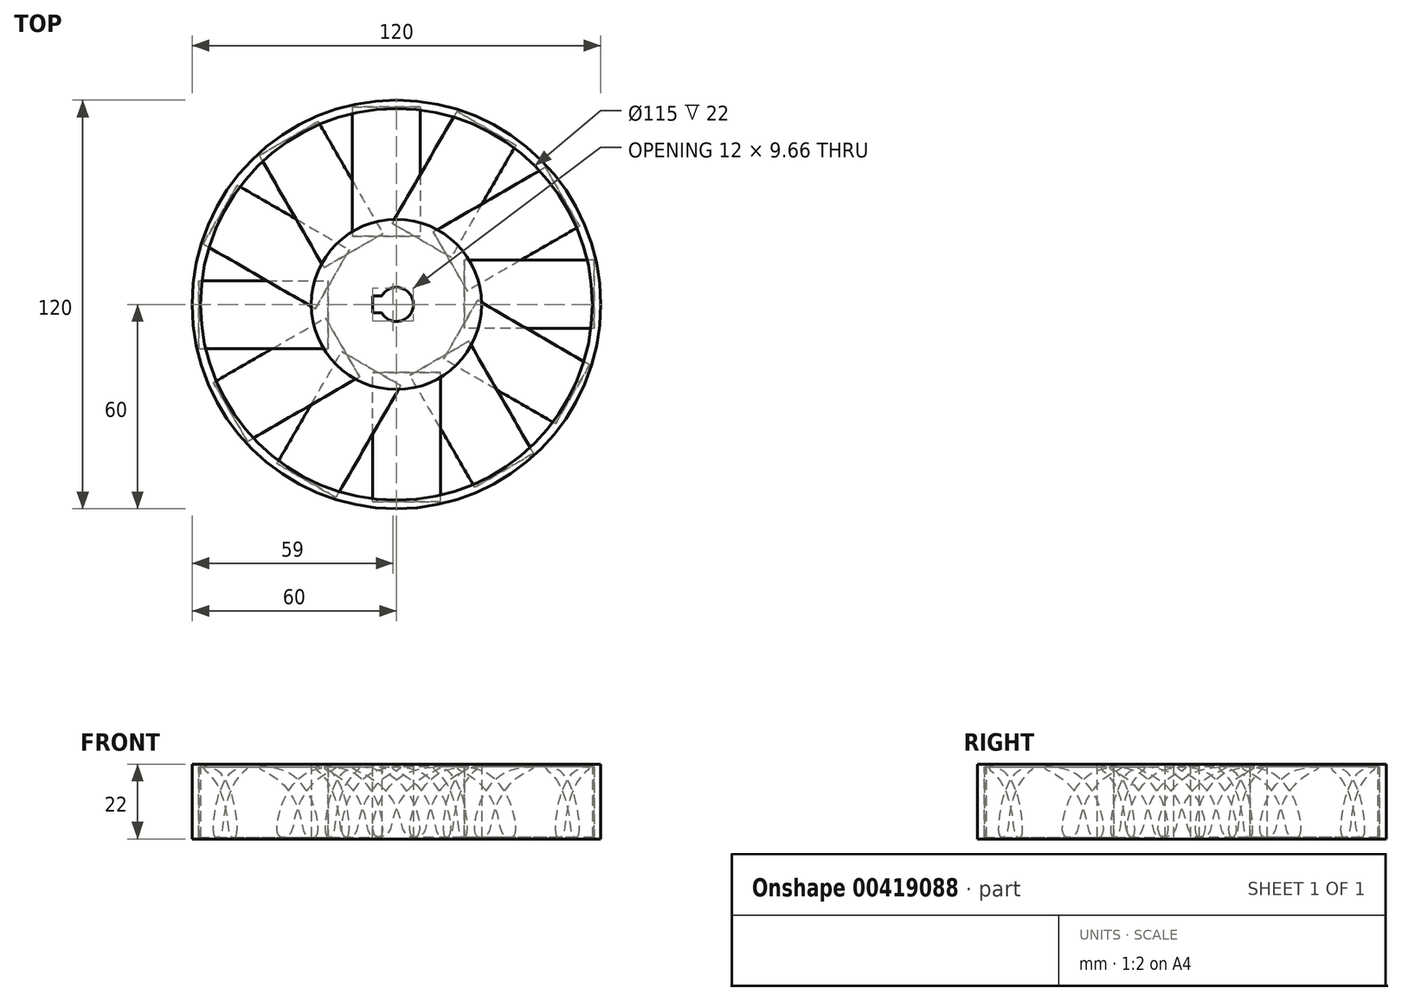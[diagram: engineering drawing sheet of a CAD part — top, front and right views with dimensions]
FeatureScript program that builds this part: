
annotation { "Feature Type Name" : "Feature", "Feature Type Description" : "" }
export const myFeature = defineFeature(function(context is Context, id is Id, definition is map)
    precondition{}
    {
        {
            var Q0;
            Q0=qCreatedBy(makeId("Right.planeOp"),FACE);
            cPlane(context, id + "F0", {"entities" : qUnion([Q0]), "cplaneType" : CPlaneType.OFFSET, "offset" : 20 * mm, "width" : 150 * mm, "height" : 150 * mm});
        }
        {
            var Q0;
            Q0=qCreatedBy(id+"F0.planeOp",FACE);
            var sketch = newSketch(context, id + "F1", { "sketchPlane" : qUnion([Q0])});
            skFitSpline(sketch, "E0", {"points": [v(-6.36, -10) * mm, v(-5.7, -1.84) * mm, v(-2.19, 4.22) * mm, v(4.69, 9.05) * mm, v(12.99, 10) * mm, v(6.5, 6.35) * mm, v(-0.88, -4.38) * mm, v(-2.84, -9.78) * mm, v(-6.36, -10) * mm]});
            skSolve(sketch);
        }
        {
            var Q0;
            Q0=makeQuery(id+"F1.imprint","IMPRINT",FACE,{"disambiguationData":[TD([[makeQuery(id+"F1.imprint","IMPRINT",EDGE,{"derivedFrom":sQuery(id+"F1.wireOp",EDGE,"E0")}),-1.0]])]});
            extrude(context, id + "F2", {"entities" : qUnion([Q0]), "depth" : 38 * mm});
        }
        {
            var Q0;
            Q0=qCreatedBy(makeId("Right.planeOp"),FACE);
            var sketch = newSketch(context, id + "F3", { "sketchPlane" : qUnion([Q0])});
            skLineSegment(sketch, "E1", {"start": v(0, 0) * mm, "end": v(0, 95.22) * mm, "construction": true});
            skSolve(sketch);
        }
        {
            var Q0;
            Q0=makeQuery(id+"F2.opExtrude","SWEPT_BODY",BODY,{"disambiguationData":[OSD([sQuery(id+"F1.wireOp",EDGE,"E0")])]});
            var Q1;
            Q1=sQuery(id+"F3.wireOp",EDGE,"E1");
            circularPattern(context, id + "F4", {"entities" : qUnion([Q0]), "axis" : qUnion([Q1]), "angle" : 360 * degree, "instanceCount" : 12, "equalSpace" : true});
        }
        {
            var Q0;
            Q0=qCreatedBy(makeId("Top.planeOp"),FACE);
            var sketch = newSketch(context, id + "F5", { "sketchPlane" : qUnion([Q0])});
            skCircle(sketch, "E2", {"center": v(0, 0) * mm, "radius": 25 * mm});
            skCircle(sketch, "E3", {"center": v(0, 0) * mm, "radius": 5 * mm});
            skCircle(sketch, "E4", {"center": v(0, 0) * mm, "radius": 57.5 * mm});
            skCircle(sketch, "E5", {"center": v(0, 0) * mm, "radius": 60 * mm});
            skSolve(sketch);
        }
        {
            var Q0;
            Q0=makeQuery(id+"F5.imprint","IMPRINT",FACE,{"disambiguationData":[TD([[makeQuery(id+"F5.imprint","IMPRINT",EDGE,{"derivedFrom":sQuery(id+"F5.wireOp",EDGE,"E4")}),-1.0]])]});
            var Q1;
            Q1=makeQuery(id+"F5.imprint","IMPRINT",FACE,{"disambiguationData":[TD([[makeQuery(id+"F5.imprint","IMPRINT",EDGE,{"derivedFrom":sQuery(id+"F5.wireOp",EDGE,"E2")}),1.0]])]});
            extrude(context, id + "F6", {"entities" : qUnion([Q0, Q1]), "endBound" : BoundingType.SYMMETRIC, "depth" : 22 * mm});
        }
        {
            var Q0;
            Q0=qCreatedBy(makeId("Top.planeOp"),FACE);
            var sketch = newSketch(context, id + "F7", { "sketchPlane" : qUnion([Q0])});
            skLineSegment(sketch, "E6.bottom", {"start": v(0, 0) * mm, "end": v(-7, 0) * mm});
            skLineSegment(sketch, "E6.top", {"start": v(0, -2.5) * mm, "end": v(-7, -2.5) * mm});
            skLineSegment(sketch, "E6.left", {"start": v(0, 0) * mm, "end": v(0, -2.5) * mm});
            skLineSegment(sketch, "E6.right", {"start": v(-7, 0) * mm, "end": v(-7, -2.5) * mm});
            skLineSegment(sketch, "E7.MirrorCS", {"start": v(0, 2.5) * mm, "end": v(-7, 2.5) * mm});
            skLineSegment(sketch, "E8.MirrorCS", {"start": v(0, 0) * mm, "end": v(0, 2.5) * mm});
            skLineSegment(sketch, "E9.MirrorCS", {"start": v(-7, 0) * mm, "end": v(-7, 2.5) * mm});
            skSolve(sketch);
        }
        {
            var Q0;
            Q0=makeQuery(id+"F7.imprint","IMPRINT",FACE,{"disambiguationData":[TD([[makeQuery(id+"F7.imprint","IMPRINT",EDGE,{"derivedFrom":sQuery(id+"F7.wireOp",EDGE,"E6.bottom")}),1.0]])]});
            var Q1;
            Q1=makeQuery(id+"F7.imprint","IMPRINT",FACE,{"disambiguationData":[TD([[makeQuery(id+"F7.imprint","IMPRINT",EDGE,{"derivedFrom":sQuery(id+"F7.wireOp",EDGE,"E6.bottom")}),-1.0]])]});
            extrude(context, id + "F8", {"entities" : qUnion([Q0, Q1]), "operationType" : NewBodyOperationType.REMOVE, "endBound" : BoundingType.SYMMETRIC, "oppositeDirection" : true, "depth" : 30 * mm});
        }
    });
